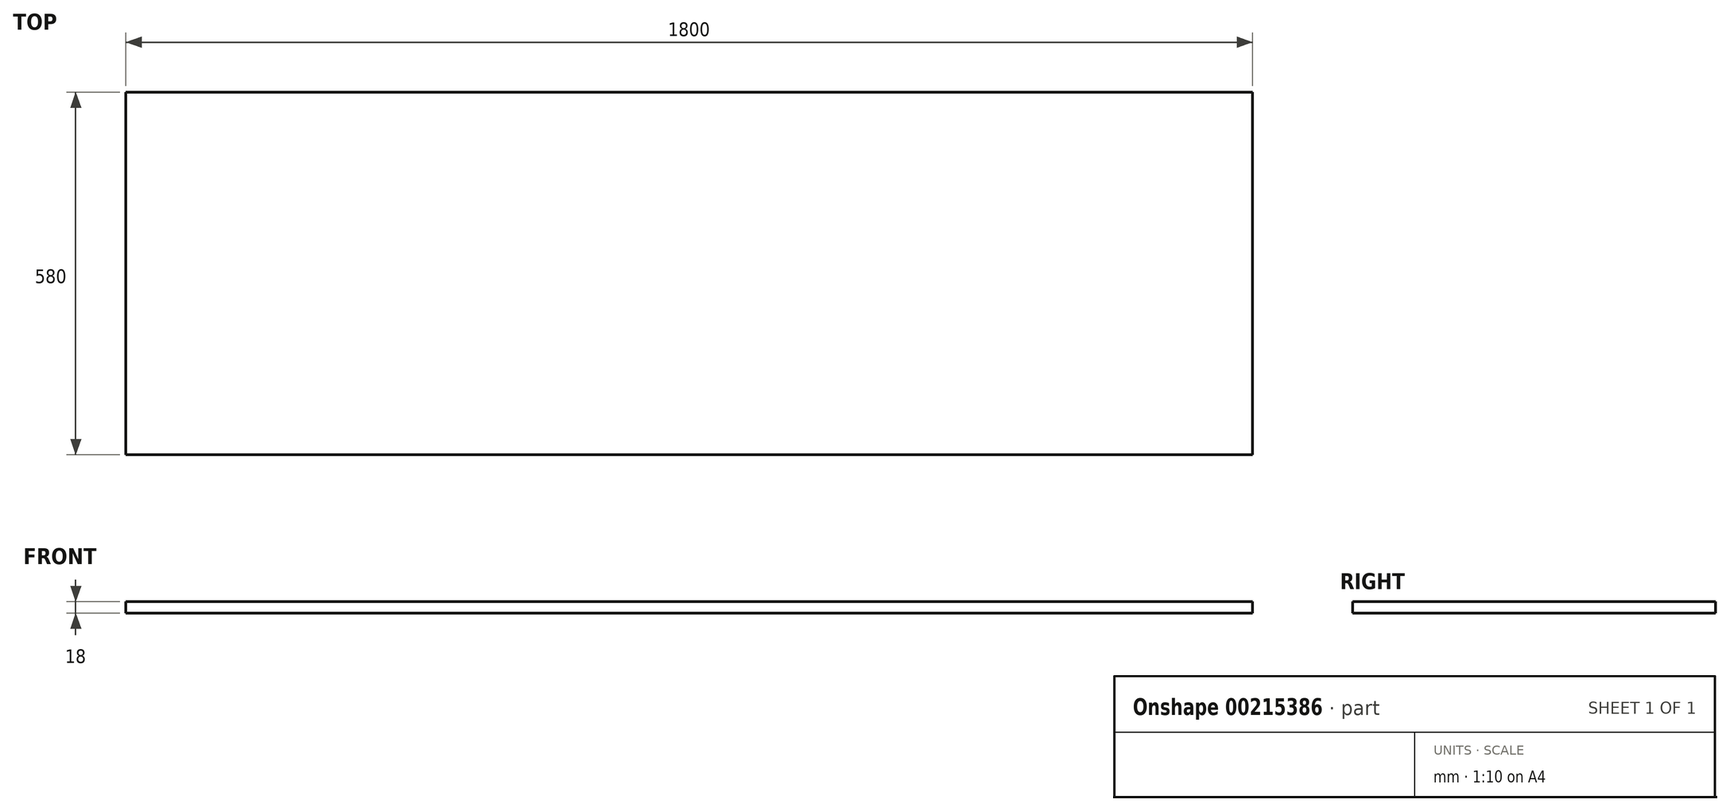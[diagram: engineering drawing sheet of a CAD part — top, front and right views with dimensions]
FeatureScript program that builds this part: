
annotation { "Feature Type Name" : "Feature", "Feature Type Description" : "" }
export const myFeature = defineFeature(function(context is Context, id is Id, definition is map)
    precondition{}
    {
        {
            var Q0;
            Q0=qCreatedBy(makeId("Top.planeOp"),FACE);
            var sketch = newSketch(context, id + "F0", { "sketchPlane" : qUnion([Q0])});
            skLineSegment(sketch, "E0.bottom", {"start": v(-900, 290) * mm, "end": v(900, 290) * mm});
            skLineSegment(sketch, "E0.top", {"start": v(-900, -290) * mm, "end": v(900, -290) * mm});
            skLineSegment(sketch, "E0.left", {"start": v(-900, 290) * mm, "end": v(-900, -290) * mm});
            skLineSegment(sketch, "E0.right", {"start": v(900, 290) * mm, "end": v(900, -290) * mm});
            skPoint(sketch, "E0.middle", {"position": v(0, 0) * mm});
            skSolve(sketch);
        }
        {
            var Q0;
            Q0=makeQuery(id+"F0.imprint","IMPRINT",FACE,{"disambiguationData":[TD([[makeQuery(id+"F0.imprint","IMPRINT",EDGE,{"derivedFrom":sQuery(id+"F0.wireOp",EDGE,"E0.bottom")}),-1.0]])]});
            extrude(context, id + "F1", {"entities" : qUnion([Q0]), "depth" : 18 * mm});
        }
    });
